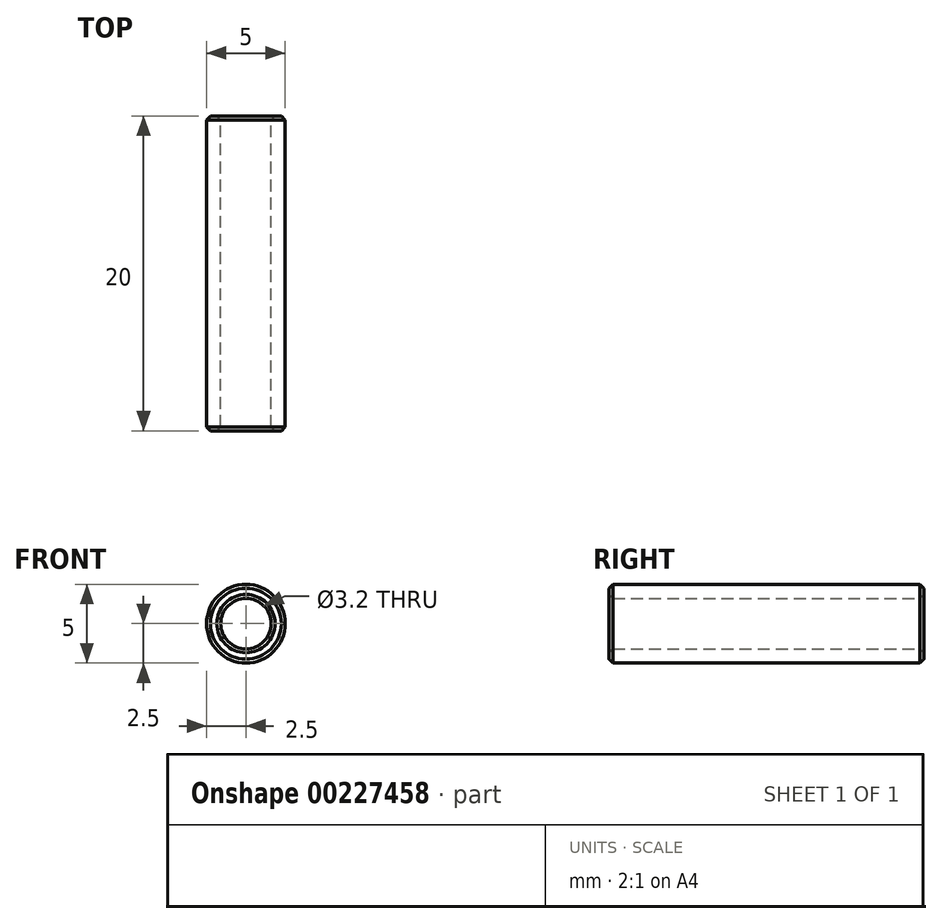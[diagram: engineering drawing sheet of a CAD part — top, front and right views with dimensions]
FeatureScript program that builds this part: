
annotation { "Feature Type Name" : "Feature", "Feature Type Description" : "" }
export const myFeature = defineFeature(function(context is Context, id is Id, definition is map)
    precondition{}
    {
        {
            var Q0;
            Q0=qCreatedBy(makeId("Front.planeOp"),FACE);
            var sketch = newSketch(context, id + "F0", { "sketchPlane" : qUnion([Q0])});
            skCircle(sketch, "E0", {"center": v(0, 0) * mm, "radius": 1.6 * mm});
            skCircle(sketch, "E1", {"center": v(0, 0) * mm, "radius": 2.5 * mm});
            skSolve(sketch);
        }
        {
            var Q0;
            Q0=makeQuery(id+"F0.imprint","IMPRINT",FACE,{"disambiguationData":[TD([[makeQuery(id+"F0.imprint","IMPRINT",EDGE,{"derivedFrom":sQuery(id+"F0.wireOp",EDGE,"E0")}),-1.0]])]});
            extrude(context, id + "F1", {"entities" : qUnion([Q0]), "depth" : 20 * mm, "symmetric" : true});
        }
        {
            var Q0;
            Q0=makeQuery(id+"F1.opExtrude","CAP_EDGE",EDGE,{"disambiguationData":[OSD([sQuery(id+"F0.wireOp",EDGE,"E1")])],"isStart":false});
            var Q1;
            Q1=makeQuery(id+"F1.opExtrude","CAP_EDGE",EDGE,{"disambiguationData":[OSD([sQuery(id+"F0.wireOp",EDGE,"E0")])],"isStart":false});
            var Q2;
            Q2=makeQuery(id+"F1.opExtrude","CAP_EDGE",EDGE,{"disambiguationData":[OSD([sQuery(id+"F0.wireOp",EDGE,"E1")])],"isStart":true});
            var Q3;
            Q3=makeQuery(id+"F1.opExtrude","CAP_EDGE",EDGE,{"disambiguationData":[OSD([sQuery(id+"F0.wireOp",EDGE,"E0")])],"isStart":true});
            chamfer(context, id + "F2", {"entities" : qUnion([Q0, Q1, Q2, Q3]), "width" : 0.25 * mm, "tangentPropagation" : true});
        }
    });
